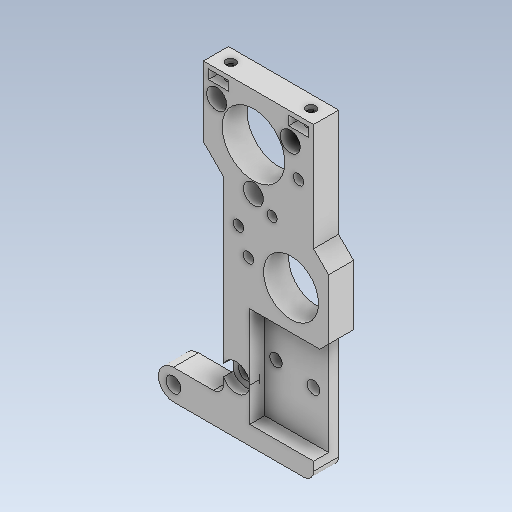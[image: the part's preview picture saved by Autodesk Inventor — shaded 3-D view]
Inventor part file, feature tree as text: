
AUTODESK INVENTOR PART (.ipt)
format: ipt  version: 2020.2 (Build 242310000, 310)  size: 387,072 bytes
history: native  units: mm
features: extrude x7, sketch x6, fillet x2, thread x2, projected_geometry x2
ambient origin geometry x8: Origin, YZ Plane, XZ Plane, XY Plane, X Axis, Y Axis, Z Axis, Center Point
bodies: Solid1 (feature_tree)
feature tree (19):
  extrude  "Extrusion1"  Depth=6.0mm
  fillet  "Fillet1"  Radius=28.0mm
  fillet  "Fillet2"  Radius=6.0mm
  extrude  "Extrusion2"  Depth=3.0mm
  extrude  "Extrusion3"  Depth=56.0mm
  thread  "Thread1"  [1 undecoded]
  thread  "Thread2"  [1 undecoded]
  extrude  "Extrusion4"  Depth=12.5mm
  extrude  "Extrusion5"  Depth=2.1mm
  extrude  "Extrusion6"  Depth=1.8mm TaperAngle=360.0deg
  extrude  "Extrusion7"  Depth=4.0mm
  sketch  "Sketch1"  dims[d0=3.0mm d1=6.0mm d2=28.0mm d3=6.0mm]
  sketch  "Sketch3"  dims[d4=0.0mm d5=3.0mm]
  projected_geometry  "Projected Loop1"
  sketch  "Sketch5"  dims[d6=18.0mm d7=56.0mm d8=11.0mm d9=4.5mm]
  sketch  "Sketch7"  dims[d10=25.5mm d11=12.5mm]
  sketch  "Sketch8"  dims[d12=22.3mm d14=2.1mm]
  projected_geometry  "Projected Loop2"
  sketch  "Sketch10"  dims[d17=9.5mm d18=30.0mm d20=360.0deg d22=4.0mm d23=14.0mm d24=45.0deg d25=3.0mm d26=12.0mm d27=6.0mm d28=135.0deg d29=135.0deg d30=5.0mm d31=0.0mm d32=3.0mm d33=10.5mm d34=2.5mm d35=2.5mm d36=14.5mm d37=7.5mm d38=2.5mm d39=15.0mm d40=13.5mm d41=2.0mm d42=2.0mm d43=12.75mm d44=20.0mm d45=23.75mm d46=3.0mm d47=0.0mm d48=2.0mm d49=2.0mm d50=2.5mm d51=2.5mm d52=3.0mm d53=3.0mm d54=3.0mm d55=0.0mm d56=7.0mm d57=0.0mm d58=7.0mm d59=0.0mm d60=8.5mm d61=270.0deg d62=4.0mm d63=4.0mm d64=4.0mm d65=3.0mm d66=0.0mm d67=5.5mm d68=2.0mm d69=0.0mm d70=4.0mm d71=1.85mm d72=4.0mm d73=1.85mm d74=1.0mm d75=1.8mm d76=1.8mm d77=1.0mm d78=10.0mm d79=0.0mm d82=2.0mm d83=11.15mm d84=2.1mm d85=2.1mm d86=2.1mm d87=5.0mm d88=3.0mm d89=25.0mm d90=29.5mm d91=3.0mm d92=11.0mm d93=24.0mm d94=8.0mm d95=2.1mm d96=2.1mm d98=2.1mm d99=1.8mm d100=0.0mm d101=2.1mm d102=2.1mm d80=0.5mm d81=0.872665mm d103=0.5mm d104=0.872665mm d105=0.5mm d106=0.872665mm]
note: 2 required parameter values undecoded (feature->parameter linkage not recoverable at this tier; creation-order binding heuristic only, values carry confidence <= 0.55)
